# Revit family: BasinMixer_Countertop_Vitra_SolidSSeries_A42440
name_source: partatom
category: Plumbing Fixtures
revit_build: Autodesk Revit 2017 (Build: 20160225_1515(x64)
units: mm (PartAtom-declared; Revit-internal decimal feet)

## family parameters
Cut with Voids When Loaded = No
Host = Face
OmniClass Number = 23.45.55.17
OmniClass Title = Mixing Faucets
Part Type = Normal
Room Calculation Point = No
Round Connector Dimension = Use Diameter
Shared = Yes

## types (10) — shared parameters
BIMobject category = Taps & Mixers
CW Connection = Yes
Coating Material = Chrome
Color = Chrome
Default Elevation = 850 mm  [stored 2.78871 ft]
Depth(mm) = 160 mm
Description = Solid S Basin Mixer
Design country = Turkey
Flow Rate(L/min. - 3 bar) = 9 L/min.
HW Connection = Yes
Height(mm) = 180 mm  [stored 0.590551 ft]
Hot Water Supply (max.) = 80 °C
Hot Water temperature, factory set to = 38 °C
IFC Classification = Sanitary Terminal
Main Material = Brass
Manufacturer = Vitra
Manufacturer name = Vitra
Masterformat 2014 Code = 22 40 00
Masterformat 2014 Description = Plumbing Fixtures
Min. flow pressure of = 0.5 bar
MountingType = Countertop
NBS Referans Code = 45-35-70/371
NBS Referans Description = Water supply fittings for wash basins and troughs
Nominal height = 0.000
Nominal width = 0.000
Number Of Connections = 2 mm  [stored 0.00656168 ft]
OmniClass Code = 23.45.55.17
OmniClass Description = Mixing Faucets
Product Properties = Energy Saving, Water Saving
Product Type = Basin Mixer
Product certification = https://vitraglobal.com
Product family = Solid S
Product group = Solid S Basin Mixer
Range of Hot Water Supply = 5 - 65 °C
Range of flow pressure = 1 - 5 bar
Test Pressure = 16 bar
UNSPSC Code = 301815
URL = https://vitraglobal.com
Uniclass 1.4 Code = L725111
Uniclass 1.4 Description = Mixer taps
Uniclass 2.0 Code = Pr_40_30_96_98
Uniclass 2.0 Description = Washbasin Tap
Uniclass 2015 Code = Pr_40_20_87_98
Uniclass 2015 Name = Washbasin Tap
Uniformat II Code = 22 40 00
Uniformat II Description = Plumbing Fixture
Weight Net (kg) = 1,336
Width(mm) = 50 mm  [stored 0.164042 ft]
Youtube = https://www.youtube.com
zero-valued in all types: Cost

## per-type parameters (varying)
| type | Article No. (default) | Brand | Connection Diameter (mm) | Model | Product SKU | Product data url | Technical description | Warranty Period (Year) |
| BasinMixer-Countertop-Vitra-SolidSSeries-A42440 | A42440 | Artema | 10 mm  [stored 0.0328084 ft] | A42440 | A42440 | https://www.vitra.com.tr | https://www.vitra.com.tr | 10 Years |
| BasinMixer-Countertop-Vitra-SolidSSeries-A42440EKF | A42440EKF |  | 10 mm  [stored 0.0328084 ft] | A42440EKF | A42440EKF | https://www.vitra.com.tr | https://www.vitra.com.tr | 7 Years |
| BasinMixer-Countertop-Vitra-SolidSSeries-A42440EKM | A42440EKM |  | 10 mm  [stored 0.0328084 ft] | A42440EKM | A42440EKM | https://www.vitra.com.tr | https://www.vitra.com.tr | 7 Years |
| BasinMixer-Countertop-Vitra-SolidSSeries-A42440ENG | A42440ENG |  | 10 mm  [stored 0.0328084 ft] | A42440ENG | A42440ENG | https://www.vitra.com.tr | https://www.vitra.com.tr | 7 Years |
| BasinMixer-Countertop-Vitra-SolidSSeries-A42440EXP | A42440EXP |  | 10 mm  [stored 0.0328084 ft] | A42440EXP | A42440EXP | https://www.vitra.com.tr | https://www.vitra.com.tr | 7 Years |
| BasinMixer-Countertop-Vitra-SolidSSeries-A42440IND | A42440IND |  | 15 mm  [stored 0.0492126 ft] | A42440IND | A42440IND | https://www.vitra-india.com | https://www.vitra-india.com | 7 Years |
| BasinMixer-Countertop-Vitra-SolidSSeries-A42440INV | A42440INV |  | 15 mm  [stored 0.0492126 ft] | A42440INV | A42440INV | https://www.vitra-india.com | https://www.vitra-india.com | 7 Years |
| BasinMixer-Countertop-Vitra-SolidSSeries-A42440TPX | A42440TPX |  | 10 mm  [stored 0.0328084 ft] | A42440TPX | A42440TPX | https://www.vitra-india.com | https://www.vitra-india.com | 7 Years |
| BasinMixer-Countertop-Vitra-SolidSSeries-A42440VUK | A42440VUK |  | 15 mm  [stored 0.0492126 ft] | A42440VUK | A42440VUK | https://www.vitra.co.uk | https://www.vitra.co.uk | 10 Years |
| BasinMixer-Countertop-Vitra-SolidSSeries-A42440ENGX | A42440ENGX |  | 10 mm  [stored 0.0328084 ft] | A42440ENGX | A42440ENGX | https://www.vitra.com.tr | https://www.vitra.com.tr | 7 Years |

note: [stored X ft] marks values corroborated as IEEE doubles in the binary element streams (Revit-internal decimal feet)

## geometry (parser evidence)
native form markers: Sweep x3
no freeform markers — native parametric forms only
